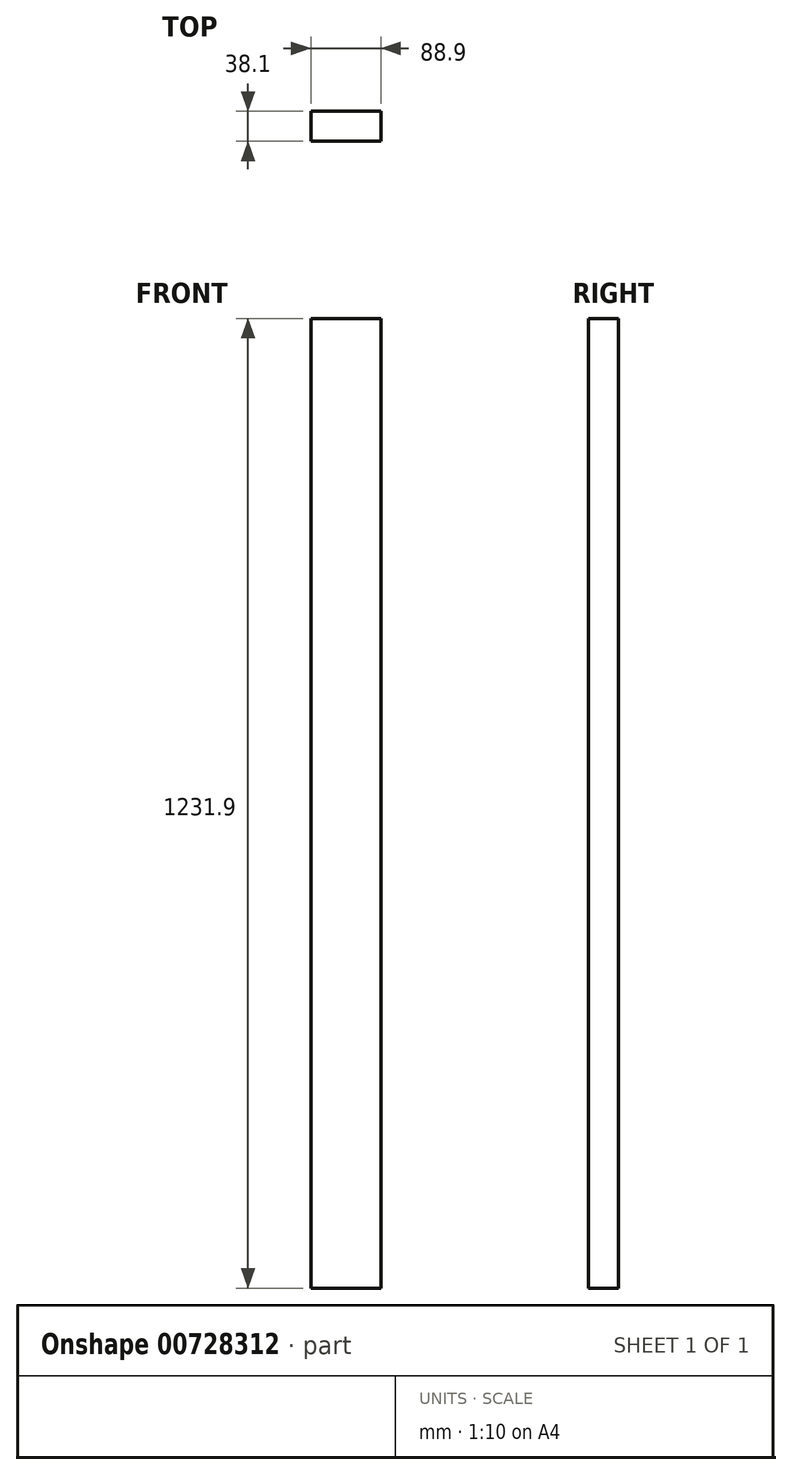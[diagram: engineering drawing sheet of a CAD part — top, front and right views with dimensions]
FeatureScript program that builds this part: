
annotation { "Feature Type Name" : "Feature", "Feature Type Description" : "" }
export const myFeature = defineFeature(function(context is Context, id is Id, definition is map)
    precondition{}
    {
        {
            var Q0;
            Q0=qCreatedBy(makeId("Front.planeOp"),FACE);
            var sketch = newSketch(context, id + "F0", { "sketchPlane" : qUnion([Q0])});
            skLineSegment(sketch, "E0.bottom", {"start": v(-44.45, -615.95) * mm, "end": v(44.45, -615.95) * mm});
            skLineSegment(sketch, "E0.top", {"start": v(-44.45, 615.95) * mm, "end": v(44.45, 615.95) * mm});
            skLineSegment(sketch, "E0.left", {"start": v(-44.45, -615.95) * mm, "end": v(-44.45, 615.95) * mm});
            skLineSegment(sketch, "E0.right", {"start": v(44.45, -615.95) * mm, "end": v(44.45, 615.95) * mm});
            skPoint(sketch, "E0.middle", {"position": v(0, 0) * mm});
            skSolve(sketch);
        }
        {
            var Q0;
            Q0=qSketchRegion(id+"F0",true);
            extrude(context, id + "F1", {"entities" : qUnion([Q0]), "depth" : 38.1 * mm});
        }
    });
